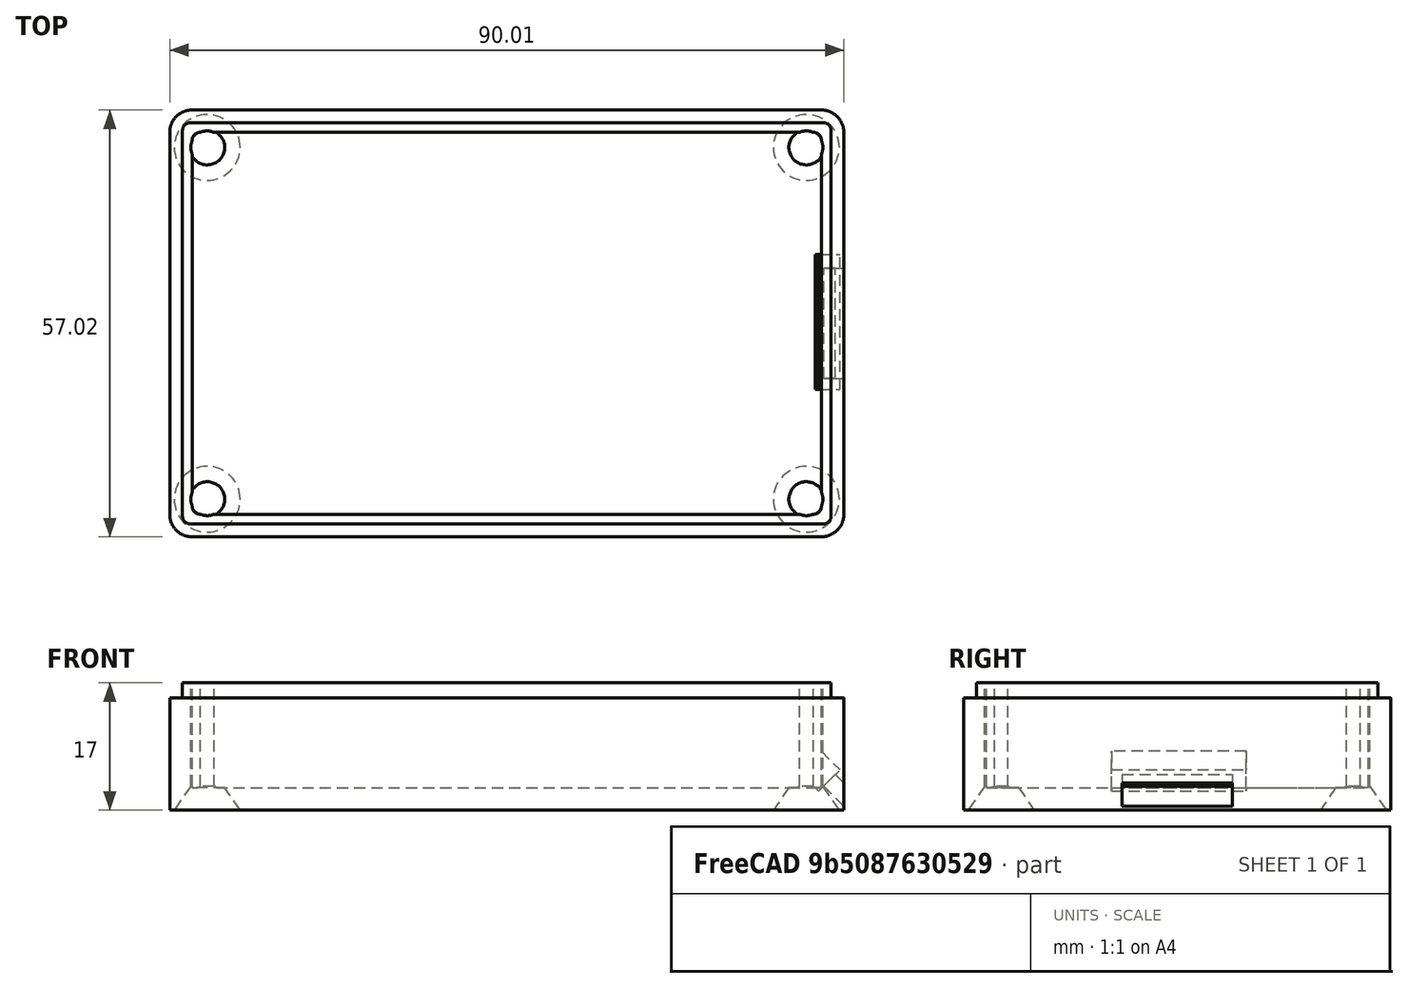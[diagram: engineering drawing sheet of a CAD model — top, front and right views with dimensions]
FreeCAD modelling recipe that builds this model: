
FCSTD DOCUMENT  (FreeCAD 0.18.4R)
Label: BoxBottomGateway
License: All rights reserved
LicenseURL: http://en.wikipedia.org/wiki/All_rights_reserved
objects: Part::Box×7, Part::MultiFuse×7, Part::Cut×4, Part::Cylinder×4, Part::Cone×4, Sketcher::SketchObject×1, PartDesign::Pad×1, Part::Fillet×1, Mesh::Feature×1
note: 30 computed .brp shape members not serialized (recipe doc carries the construction recipe); baked Part::Feature solids carry a one-line shape summary decoded from their .brp

FEATURE [Sketcher::SketchObject] Sketch002
  MapMode = 5
  sketch-geometry (8):
    g0: LineSegment StartX=13.9991 StartY=-28.0179 StartZ=0 EndX=-70.0273 EndY=-28.0179 EndZ=0
    g1: LineSegment StartX=-73.0069 StartY=-25.0383 StartZ=0 EndX=-73.0069 EndY=26.018 EndZ=0
    g2: LineSegment StartX=-70.0215 StartY=29.0034 StartZ=0 EndX=14.0112 EndY=29.0034 EndZ=0
    g3: LineSegment StartX=16.9985 StartY=26.0161 StartZ=0 EndX=16.9985 EndY=-25.0185 EndZ=0
    g4: ArcOfCircle CenterX=13.9991 CenterY=-25.0185 CenterZ=0 NormalX=0 NormalY=0 NormalZ=1 AngleXU=0 Radius=2.99936 StartAngle=4.71239 EndAngle=6.28319
    g5: ArcOfCircle CenterX=-70.0273 CenterY=-25.0383 CenterZ=0 NormalX=0 NormalY=0 NormalZ=1 AngleXU=0 Radius=2.97959 StartAngle=3.14159 EndAngle=4.71239
    g6: ArcOfCircle CenterX=-70.0215 CenterY=26.018 CenterZ=0 NormalX=0 NormalY=0 NormalZ=1 AngleXU=0 Radius=2.98541 StartAngle=1.5708 EndAngle=3.14159
    g7: ArcOfCircle CenterX=14.0112 CenterY=26.0161 CenterZ=0 NormalX=0 NormalY=0 NormalZ=1 AngleXU=0 Radius=2.98728 StartAngle=1.028e-13 EndAngle=1.5708
  constraints (12):
    c: Horizontal(g0)
    c: Horizontal(g2)
    c: Vertical(g1)
    c: Vertical(g3)
    c: Tangent(g3,g4) = 1.5708
    c: Tangent(g0,g4) = 1.5708
    c: Tangent(g1,g5) = 1.5708
    c: Tangent(g0,g5) = 1.5708
    c: Tangent(g1,g6) = 1.5708
    c: Tangent(g2,g6) = 1.5708
    c: Tangent(g2,g7) = 1.5708
    c: Tangent(g3,g7) = 1.5708
FEATURE [PartDesign::Pad] Pad013
  Length = 17
  Length2 = 100
  Profile = -> Sketch002
  Type = 0
FEATURE [Part::Box] Box010  label="Würfel010"
  AttacherType = Attacher::AttachEngine3D
  Height = 25
  Length = 84
  Placement = pos=(-70,-25,3) rot=(0,0,1;0rad)
  Width = 51
FEATURE [Part::Cut] Cut011  label="Box raw"
  Base = -> Pad013
  Tool = -> Box010
FEATURE [Part::Box] Box  label="Rand002"
  AttacherType = Attacher::AttachEngine3D
  Height = 2
  Length = 90
  Placement = pos=(-73,27.3,14) rot=(0,0,1;0rad)
  Width = 2
FEATURE [Part::Box] Box011  label="Rand001"
  AttacherType = Attacher::AttachEngine3D
  Height = 2
  Length = 90
  Placement = pos=(-73,-28.3,14) rot=(0,0,1;0rad)
  Width = 2
FEATURE [Part::Box] Box012  label="Rand003"
  AttacherType = Attacher::AttachEngine3D
  Height = 2
  Length = 2
  Placement = pos=(-73.3,-28,14) rot=(0,0,1;0rad)
  Width = 57
FEATURE [Part::Box] Box013  label="Rand004"
  AttacherType = Attacher::AttachEngine3D
  Height = 2
  Length = 2
  Placement = pos=(15.3,-28,14) rot=(0,0,1;0rad)
  Width = 57
FEATURE [Part::MultiFuse] Fusion  label="RandFraesung"
  Placement = pos=(0,0,1) rot=(0,0,1;0rad)
  Shapes = -> [Box013,Box012,Box011,Box]
FEATURE [Part::Box] Box018  label="Kabeltunnel"
  AttacherType = Attacher::AttachEngine3D
  Height = 2.2
  Length = 10
  Placement = pos=(12,-6.85,5.5) rot=(0,1,0;0.785398rad)
  Width = 14.7
FEATURE [Part::Cylinder] Cylinder005  label="Zylinder"
  Angle = 360
  AttacherType = Attacher::AttachEngine3D
  Height = 18
  Placement = pos=(12,-23,-1) rot=(0,0,1;0rad)
  Radius = 2.2
FEATURE [Part::Cone] Cone  label="Kegel"
  Angle = 360
  AttacherType = Attacher::AttachEngine3D
  Height = 3.2
  Placement = pos=(12,-23,-1) rot=(0,0,1;0rad)
  Radius1 = 4.4
  Radius2 = 2.2
FEATURE [Part::MultiFuse] Fusion002  label="Bohrung001"
  Placement = pos=(0,0,1) rot=(0,0,1;0rad)
  Shapes = -> [Cylinder005,Cone]
FEATURE [Part::Cylinder] Cylinder006  label="Zylinder003"
  Angle = 360
  AttacherType = Attacher::AttachEngine3D
  Height = 18
  Placement = pos=(12,-23,-1) rot=(0,0,1;0rad)
  Radius = 2.2
FEATURE [Part::Cone] Cone001  label="Kegel001"
  Angle = 360
  AttacherType = Attacher::AttachEngine3D
  Height = 3.2
  Placement = pos=(12,-23,-1) rot=(0,0,1;0rad)
  Radius1 = 4.4
  Radius2 = 2.2
FEATURE [Part::MultiFuse] Fusion003  label="Bohrung002"
  Placement = pos=(0,47,1) rot=(0,0,1;0rad)
  Shapes = -> [Cylinder006,Cone001]
FEATURE [Part::Cylinder] Cylinder007  label="Zylinder004"
  Angle = 360
  AttacherType = Attacher::AttachEngine3D
  Height = 18
  Placement = pos=(12,-23,-1) rot=(0,0,1;0rad)
  Radius = 2.2
FEATURE [Part::Cone] Cone002  label="Kegel002"
  Angle = 360
  AttacherType = Attacher::AttachEngine3D
  Height = 3.2
  Placement = pos=(12,-23,-1) rot=(0,0,1;0rad)
  Radius1 = 4.4
  Radius2 = 2.2
FEATURE [Part::MultiFuse] Fusion004  label="Bohrung003"
  Placement = pos=(-80,0,1) rot=(0,0,1;0rad)
  Shapes = -> [Cylinder007,Cone002]
FEATURE [Part::Cylinder] Cylinder008  label="Zylinder005"
  Angle = 360
  AttacherType = Attacher::AttachEngine3D
  Height = 18
  Placement = pos=(12,-23,-1) rot=(0,0,1;0rad)
  Radius = 2.2
FEATURE [Part::Cone] Cone003  label="Kegel003"
  Angle = 360
  AttacherType = Attacher::AttachEngine3D
  Height = 3.2
  Placement = pos=(12,-23,-1) rot=(0,0,1;0rad)
  Radius1 = 4.4
  Radius2 = 2.2
FEATURE [Part::MultiFuse] Fusion005  label="Bohrung004"
  Placement = pos=(-80,47,1) rot=(0,0,1;0rad)
  Shapes = -> [Cylinder008,Cone003]
FEATURE [Part::MultiFuse] Fusion006  label="Bohrungen"
  Shapes = -> [Fusion003,Fusion002,Fusion004,Fusion005]
FEATURE [Part::Box] Box019  label="KabelTunnelDichtungsSchacht"
  AttacherType = Attacher::AttachEngine3D
  Height = 4
  Length = 8
  Placement = pos=(8,-8.3,8.2) rot=(0,1,0;0.785398rad)
  Width = 18
FEATURE [Part::MultiFuse] Fusion007  label="Kabelschacht"
  Shapes = -> [Box018,Box019]
FEATURE [Part::Cut] Cut
  Base = -> Cut011
  Tool = -> Fusion
FEATURE [Part::Fillet] Fillet  label="Box fine"
  Base = -> Cut
  Edges = 8 edges r=1: [Edge40,Edge41,Edge49,Edge56,Edge57,Edge58,Edge60,Edge62]
FEATURE [Part::Cut] Cut012
  Base = -> Fillet
  Tool = -> Fusion006
FEATURE [Part::Cut] Cut013  label="Box ready"
  Base = -> Cut012
  Tool = -> Fusion007
FEATURE [Mesh::Feature] Mesh  label="Box ready (Meshed)"
